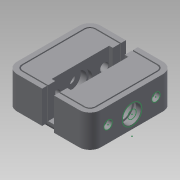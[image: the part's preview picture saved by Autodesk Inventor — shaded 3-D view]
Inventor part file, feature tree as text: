
AUTODESK INVENTOR PART (.ipt)
format: ipt  version: 2015 SP1 (Build 190203100, 203)  size: 334,848 bytes
history: native  units: mm
features: extrude x12, sketch x8, mirror x4, projected_geometry x3, fillet x2, plane x1
ambient origin geometry x8: Origin, YZ Plane, XZ Plane, XY Plane, X Axis, Y Axis, Z Axis, Center Point
bodies: Solid1 (feature_tree)
feature tree (30):
  sketch  "Sketch1"  dims[d0=30.0mm d1=30.0mm]
  extrude  "Extrusion1"  Depth=30.0mm
  extrude  "Extrusion2"  Depth=30.0mm TaperAngle=0.0deg
  extrude  "Extrusion3"  Depth=10.0mm
  sketch  "Sketch2"  dims[d2=3.0mm d3=0.0mm d4=30.0mm d5=0.0mm]
  extrude  "Extrusion6"  Depth=3.5mm
  extrude  "Extrusion7"  Depth=13.5mm TaperAngle=0.0deg
  extrude  "Extrusion8"  Depth=1.5mm
  extrude  "Extrusion9"  Depth=2.0mm
  fillet  "Fillet1"  Radius=2.0mm
  fillet  "Fillet2"  Radius=9.5mm
  plane  "Work Plane1"
  mirror  "Mirror3"
  mirror  "Mirror4"
  extrude  "Extrusion11"  Depth=0.5mm
  extrude  "Extrusion15"  Depth=2.0mm
  extrude  "Extrusion16"  Depth=2.0mm
  mirror  "Mirror7"
  extrude  "Extrusion17"  Depth=27.5mm TaperAngle=0.0deg
  extrude  "Extrusion18"  Depth=5.5mm
  mirror  "Mirror8"
  sketch  "Sketch14"  dims[d38=0.5mm d39=0.5mm d40=2.0mm d41=2.0mm d42=27.5mm d43=0.0mm d51=5.5mm d52=8.0mm d53=8.0mm d54=0.0mm d55=7.5mm d56=2.0mm d57=0.0mm d61=3.5mm d62=2.0mm d63=0.0mm d64=8.0mm d65=0.0mm]
  sketch  "Sketch6"  dims[d6=3.0mm d7=0.0mm d8=10.0mm]
  sketch  "Sketch10"  dims[d9=8.0mm d12=3.5mm]
  sketch  "Sketch11"  dims[d15=11.0mm d16=0.0mm d17=13.5mm d18=0.0mm]
  sketch  "Sketch12"  dims[d19=1.5mm d20=0.0mm d21=8.25mm]
  projected_geometry  "Projected Loop3"
  sketch  "Sketch13"  dims[d22=4.0mm d23=0.0mm d35=2.0mm d36=2.0mm d37=9.5mm]
  projected_geometry  "Projected Loop4"
  projected_geometry  "Projected Loop5"
